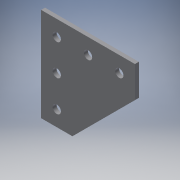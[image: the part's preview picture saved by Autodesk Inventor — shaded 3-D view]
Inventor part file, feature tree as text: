
AUTODESK INVENTOR PART (.ipt)
format: ipt  version: 2016 (Build 200138000, 138)  size: 107,520 bytes
history: native  units: in
note: dims shown in document units (in); Inventor stores cm internally (conversion verified against a paired STEP export)
features: extrude x1, sketch x1
ambient origin geometry x8: Origin, YZ Plane, XZ Plane, XY Plane, X Axis, Y Axis, Z Axis, Center Point
bodies: Solid1 (feature_tree)
feature tree (2):
  extrude  "Extrusion1"  Depth=0.125in
  sketch  "Sketch1"  dims[d0=3.0in d1=1.0in d2=0.5in d3=0.2656in d4=0.2656in d5=0.2656in d6=0.2656in d7=0.2656in d8=2.5in d9=1.0in d10=1.0in d11=1.0in d12=0.125in d13=0.0in]
